# Revit family: WH538-CSH-SRCH
name_source: partatom
category: Plumbing Fixtures
revit_build: Autodesk Revit 2018 (Build: 20170223_1515(x64)
units: mm (PartAtom-declared; Revit-internal decimal feet)

## family parameters
Cut with Voids When Loaded = No
Host = Face
OmniClass Number = 23.45.05.14.17
OmniClass Title = Showers
Part Type = Normal
Room Calculation Point = No
Round Connector Dimension = Use Diameter
Shared = Yes

## types (1)
- WH538-CSH-SRCH
    ADA Compliant = Yes
    Assembly Code = D2010710
    CW Connection = Yes
    CWFU = 3
    Cold Water Connection Diameter = 1"
    Cold Water Connection Radius = 1/2"
    Default Elevation = 72"
    Description = Ligature Resistant Shower Head and Valve
    Flange Material = Metal-Whitehalls-304 Stainless Steel White
    Flow Rate = 1.5 GPM
    HW Connection = Yes
    HWFU = 3
    Hot Water Connection Diameter = 1"
    Hot Water Connection Radius = 1/2"
    Installation Type = Wall Mounted
    Manufacturer = Whitehall Mfg.
    Model = WH538-CSH-SRCH
    Price = Prices may vary. Please consult Manufacturer Representative for most up-to-date price list.
    Product Documentation Link = https://www.whitehallmfg.com
    Product Page URL = https://www.whitehallmfg.com
    Shower Head Plate Width = 5 1/8"
    Showerhead Material = Metal-Whitehalls-Chrome Plated Brass
    Tri-Lever Handle Diameter = 5 1/2"
    Tri-Lever Handle Material = Metal-Whitehalls-Chrome Plated Brass
    URL = https://www.whitehallmfg.com
    Vent Connection = No
    WFU = 0
    Waste Connection = No

## geometry (parser evidence)
native form markers: Sweep x3
no freeform markers — native parametric forms only
